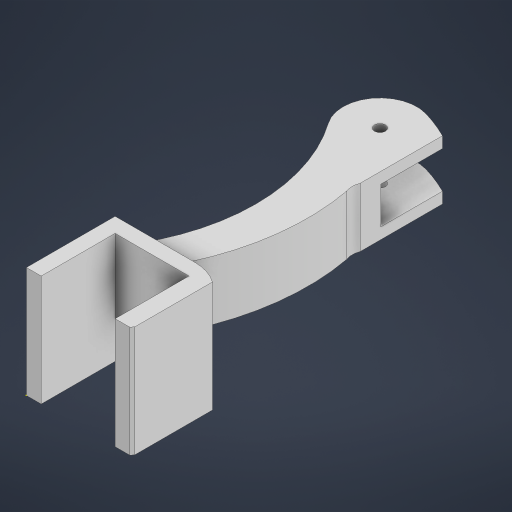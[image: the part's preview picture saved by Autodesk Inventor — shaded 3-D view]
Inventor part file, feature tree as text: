
AUTODESK INVENTOR PART (.ipt)
format: ipt  version: 2024 (Build 280153000, 153)  size: 550,912 bytes
history: native  units: mm
features: sketch x10, extrude x9, other x5, mirror x2, fillet x2
ambient origin geometry x8: Origin, YZ Plane, XZ Plane, XY Plane, X Axis, Y Axis, Z Axis, Center Point
bodies: Body1 (feature_tree)
feature tree (28):
  other  "Твердое тело1"
  extrude  "Выдавливание1"  Depth=20.0mm
  extrude  "Выдавливание2"  Depth=4.0mm
  other  "РабПлоскость1"
  extrude  "Выдавливание3"  Depth=4.0mm
  other  "shok_absorber_holder"
  extrude  "Выдавливание4"  Depth=30.0mm TaperAngle=0.0deg
  other  "РабПлоскость2"
  mirror  "Зеркальное отражение1"
  fillet  "Сопряжение1"  Radius=10.0mm
  fillet  "Сопряжение2"  Radius=3.0mm
  extrude  "Выдавливание5"  Depth=50.0mm
  extrude  "Выдавливание6"  Depth=30.0mm TaperAngle=0.0deg
  sketch  "Эскиз8"
  extrude  "Выдавливание7"  Depth=10.0mm
  mirror  "Зеркальное отражение2"
  extrude  "Выдавливание8"  Depth=20.0mm
  extrude  "Выдавливание9"  TaperAngle=0.0deg  [1 undecoded]
  sketch  "Эскиз1"
  sketch  "Эскиз2"
  sketch  "Эскиз4"
  sketch  "Эскиз5"
  sketch  "Эскиз6"
  sketch  "Эскиз7"
  sketch  "Эскиз9"
  sketch  "Эскиз10"
  sketch  "Эскиз11"
  other  "ЭлементСетки1"
note: 1 required parameter value undecoded (feature->parameter linkage not recoverable at this tier; creation-order binding heuristic only, values carry confidence <= 0.55)
